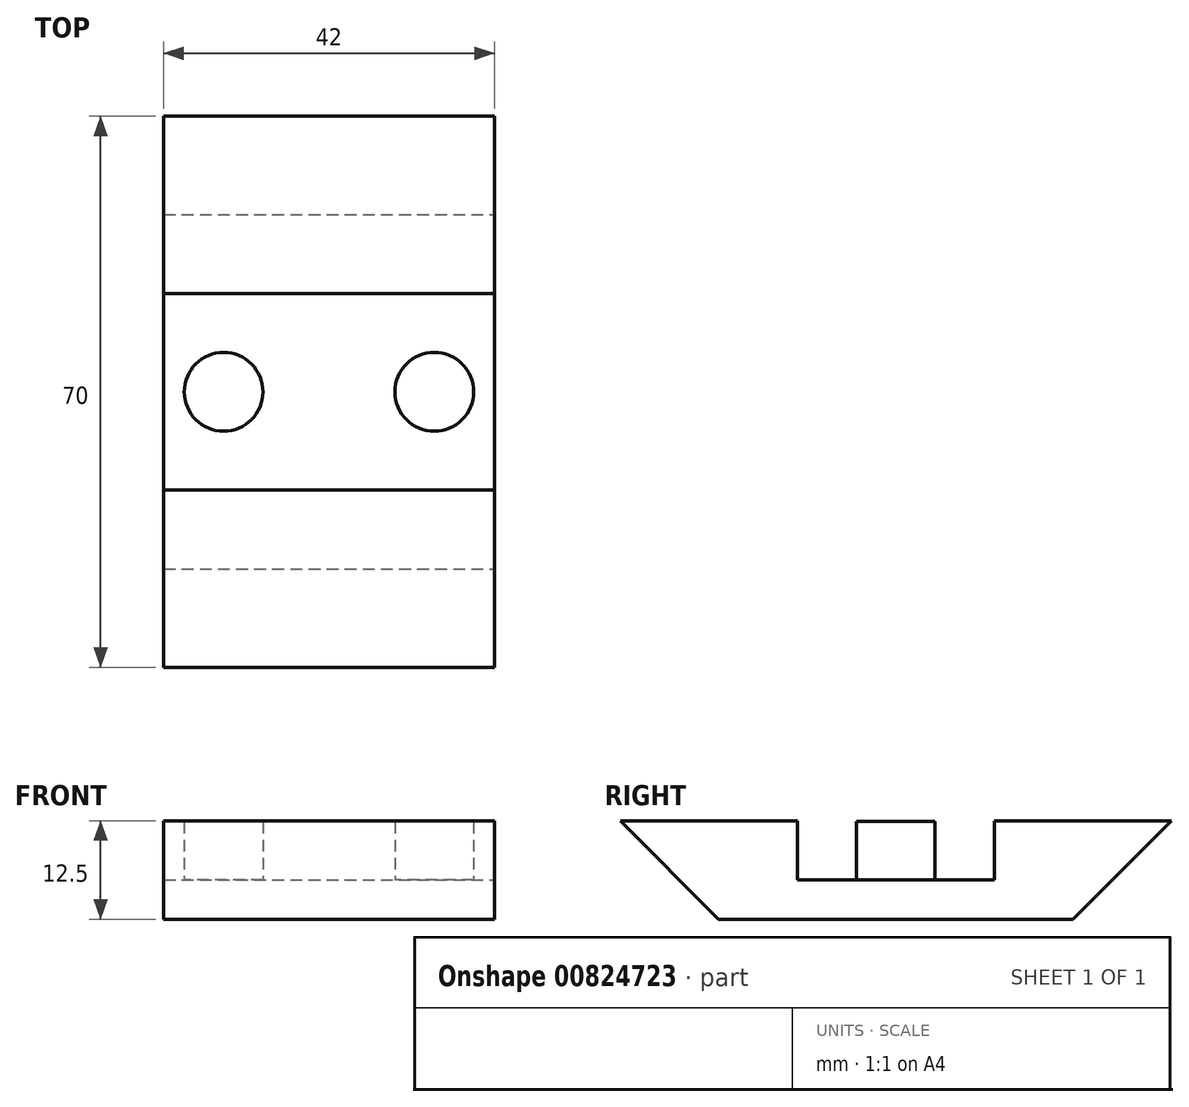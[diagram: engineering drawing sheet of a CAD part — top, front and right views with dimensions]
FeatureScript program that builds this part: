
annotation { "Feature Type Name" : "Feature", "Feature Type Description" : "" }
export const myFeature = defineFeature(function(context is Context, id is Id, definition is map)
    precondition{}
    {
        {
            var Q0;
            Q0=qCreatedBy(makeId("Top.planeOp"),FACE);
            var sketch = newSketch(context, id + "F0", { "sketchPlane" : qUnion([Q0])});
            skLineSegment(sketch, "E0.bottom", {"start": v(-21, 22.5) * mm, "end": v(21, 22.5) * mm});
            skLineSegment(sketch, "E0.top", {"start": v(-21, -22.5) * mm, "end": v(21, -22.5) * mm});
            skLineSegment(sketch, "E0.left", {"start": v(-21, 22.5) * mm, "end": v(-21, -22.5) * mm});
            skLineSegment(sketch, "E0.right", {"start": v(21, 22.5) * mm, "end": v(21, -22.5) * mm});
            skPoint(sketch, "E0.middle", {"position": v(0, 0) * mm});
            skSolve(sketch);
        }
        {
            var Q0;
            Q0=makeQuery(id+"F0.imprint","IMPRINT",FACE,{"disambiguationData":[TD([[makeQuery(id+"F0.imprint","IMPRINT",EDGE,{"derivedFrom":sQuery(id+"F0.wireOp",EDGE,"E0.bottom")}),-1.0]])]});
            extrude(context, id + "F1", {"entities" : qUnion([Q0]), "depth" : 5 * mm, "offsetDistance" : 25 * mm});
        }
        {
            var Q0;
            Q0=makeQuery(id+"F1.opExtrude","CAP_FACE",FACE,{"disambiguationData":[OSD([sQuery(id+"F0.wireOp",EDGE,"E0.bottom"),sQuery(id+"F0.wireOp",EDGE,"E0.top"),sQuery(id+"F0.wireOp",EDGE,"E0.left"),sQuery(id+"F0.wireOp",EDGE,"E0.right")])],"isStart":false});
            var sketch = newSketch(context, id + "F2", { "sketchPlane" : qUnion([Q0])});
            skCircle(sketch, "E1", {"center": v(-13.38, 0) * mm, "radius": 5 * mm});
            skCircle(sketch, "E2", {"center": v(13.38, 0) * mm, "radius": 5 * mm});
            skSolve(sketch);
        }
        {
            var Q0;
            Q0 = qSketchRegion(id + "F2", true);
            extrude(context, id + "F3", {"entities" : qUnion([Q0]), "operationType" : NewBodyOperationType.ADD, "depth" : 7.4 * mm, "offsetDistance" : 25 * mm});
        }
        {
            var Q0;
            Q0=makeQuery(id+"F1.opExtrude","CAP_FACE",FACE,{"disambiguationData":[OSD([sQuery(id+"F0.wireOp",EDGE,"E0.bottom"),sQuery(id+"F0.wireOp",EDGE,"E0.top"),sQuery(id+"F0.wireOp",EDGE,"E0.left"),sQuery(id+"F0.wireOp",EDGE,"E0.right")])],"isStart":false});
            var sketch = newSketch(context, id + "F4", { "sketchPlane" : qUnion([Q0])});
            skLineSegment(sketch, "E3.bottom", {"start": v(-21, 22.5) * mm, "end": v(21, 22.5) * mm});
            skLineSegment(sketch, "E3.top", {"start": v(-21, 12.5) * mm, "end": v(21, 12.5) * mm});
            skLineSegment(sketch, "E3.left", {"start": v(-21, 22.5) * mm, "end": v(-21, 12.5) * mm});
            skLineSegment(sketch, "E3.right", {"start": v(21, 22.5) * mm, "end": v(21, 12.5) * mm});
            skLineSegment(sketch, "E4.bottom", {"start": v(-21, -22.5) * mm, "end": v(21, -22.5) * mm});
            skLineSegment(sketch, "E4.top", {"start": v(-21, -12.5) * mm, "end": v(21, -12.5) * mm});
            skLineSegment(sketch, "E4.left", {"start": v(-21, -22.5) * mm, "end": v(-21, -12.5) * mm});
            skLineSegment(sketch, "E4.right", {"start": v(21, -22.5) * mm, "end": v(21, -12.5) * mm});
            skSolve(sketch);
        }
        {
            var Q0;
            Q0 = qSketchRegion(id + "F4", true);
            extrude(context, id + "F5", {"entities" : qUnion([Q0]), "operationType" : NewBodyOperationType.ADD, "depth" : 7.5 * mm, "offsetDistance" : 25 * mm});
        }
        {
            var Q0;
            Q0=makeQuery(id+"F5.boolean.opBoolean","MERGE",FACE,{"derivedFrom":[makeQuery(id+"F1.opExtrude","SWEPT_FACE",FACE,{"disambiguationData":[OSD([sQuery(id+"F0.wireOp",EDGE,"E0.right")])]}),makeQuery(id+"F5.opExtrude","SWEPT_FACE",FACE,{"disambiguationData":[OSD([sQuery(id+"F4.wireOp",EDGE,"E3.right")])]}),makeQuery(id+"F5.opExtrude","SWEPT_FACE",FACE,{"disambiguationData":[OSD([sQuery(id+"F4.wireOp",EDGE,"E4.right")])]})]});
            var sketch = newSketch(context, id + "F6", { "sketchPlane" : qUnion([Q0])});
            skLineSegment(sketch, "E5", {"start": v(22.5, 0) * mm, "end": v(35, 12.5) * mm});
            skLineSegment(sketch, "E6", {"start": v(35, 12.5) * mm, "end": v(22.5, 12.5) * mm});
            skLineSegment(sketch, "E7", {"start": v(22.5, 12.5) * mm, "end": v(22.5, 0) * mm});
            skSolve(sketch);
        }
        {
            var Q0;
            Q0 = qSketchRegion(id + "F6", true);
            extrude(context, id + "F7", {"entities" : qUnion([Q0]), "operationType" : NewBodyOperationType.ADD, "oppositeDirection" : true, "depth" : 42 * mm, "offsetDistance" : 25 * mm});
        }
        {
            var Q0;
            Q0=makeQuery(id+"F7.boolean.opBoolean","MERGE",FACE,{"derivedFrom":[makeQuery(id+"F5.boolean.opBoolean","MERGE",FACE,{"derivedFrom":[makeQuery(id+"F1.opExtrude","SWEPT_FACE",FACE,{"disambiguationData":[OSD([sQuery(id+"F0.wireOp",EDGE,"E0.right")])]}),makeQuery(id+"F5.opExtrude","SWEPT_FACE",FACE,{"disambiguationData":[OSD([sQuery(id+"F4.wireOp",EDGE,"E3.right")])]}),makeQuery(id+"F5.opExtrude","SWEPT_FACE",FACE,{"disambiguationData":[OSD([sQuery(id+"F4.wireOp",EDGE,"E4.right")])]})]}),makeQuery(id+"F7.opExtrude","CAP_FACE",FACE,{"disambiguationData":[OSD([sQuery(id+"F6.wireOp",EDGE,"E5"),sQuery(id+"F6.wireOp",EDGE,"E6"),sQuery(id+"F6.wireOp",EDGE,"E7")])],"isStart":true})]});
            var sketch = newSketch(context, id + "F8", { "sketchPlane" : qUnion([Q0])});
            skLineSegment(sketch, "E8", {"start": v(-22.5, 0) * mm, "end": v(-35, 12.5) * mm});
            skLineSegment(sketch, "E9", {"start": v(-35, 12.5) * mm, "end": v(-22.5, 12.5) * mm});
            skLineSegment(sketch, "E10", {"start": v(-22.5, 12.5) * mm, "end": v(-22.5, 0) * mm});
            skSolve(sketch);
        }
        {
            var Q0;
            Q0 = qSketchRegion(id + "F8", true);
            extrude(context, id + "F9", {"entities" : qUnion([Q0]), "operationType" : NewBodyOperationType.ADD, "oppositeDirection" : true, "depth" : 42 * mm, "offsetDistance" : 25 * mm});
        }
    });
